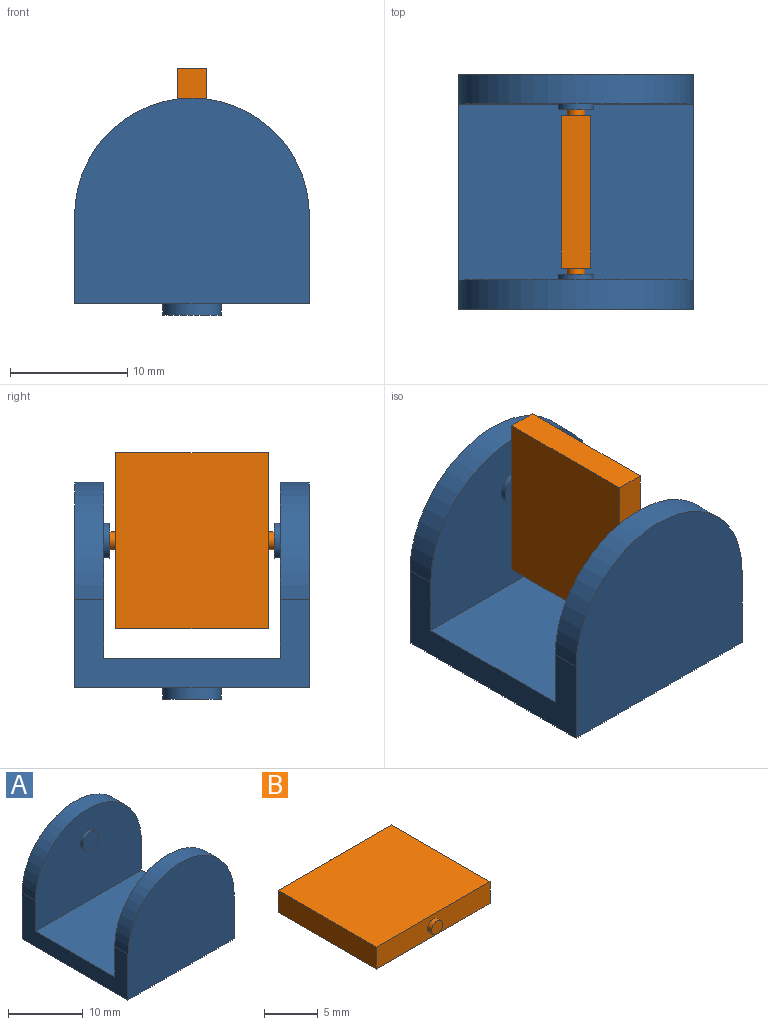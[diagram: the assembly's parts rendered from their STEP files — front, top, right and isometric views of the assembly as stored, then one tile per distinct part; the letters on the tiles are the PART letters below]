
ASSEMBLY  parts=2 mates=2
PART A: 16 faces, bbox 20x20x18.5 mm
  f0: plane 20x15mm, normal (0,0,1), area 300mm2, adj f1,f3,f6,f7
  f1: plane 20x7.5mm, normal (1,0,0), area 75mm2, adj f0,f2,f4,f5,f6,f7,f10,f11
  f2: plane 20x17.5mm, normal (0,1,0), area 307.1mm2, adj f1,f3,f5,f10
  f3: plane 20x7.5mm, normal (-1,0,0), area 75mm2, adj f0,f2,f4,f5,f6,f7,f10,f11
  f4: plane 20x17.5mm, normal (0,-1,0), area 307.1mm2, adj f1,f3,f5,f11
  f5: plane 20x20mm, normal (0,0,-1), area 380.4mm2, adj f1,f2,f3,f4,f8
  f6: plane 20x15mm, normal (0,-1,0), area 250mm2, adj f0,f1,f3,f10,f12
  f7: plane 20x15mm, normal (0,1,0), area 250mm2, adj f0,f1,f3,f11,f14
  f8: cylinder r=2.5mm len=5mm, axis (0,0,1), area 15.7mm2, adj f5,f9
  f9: plane 5x5mm, normal (0,0,-1), area 19.6mm2, adj f8
  f10: cylinder r=10mm len=20mm, axis (0,1,0), area 78.5mm2, adj f1,f2,f3,f6
  f11: cylinder r=10mm len=20mm, axis (0,1,0), area 78.5mm2, adj f1,f3,f4,f7
  f12: cylinder r=1.5mm len=3mm, axis (0,1,0), area 4.7mm2, adj f6,f13
  f13: plane 3x3mm, normal (0,-1,0), area 7.1mm2, adj f12
  f14: cylinder r=1.5mm len=3mm, axis (0,-1,0), area 4.7mm2, adj f7,f15
  f15: plane 3x3mm, normal (0,1,0), area 7.1mm2, adj f14
PART B: 10 faces, bbox 15x14x2.5 mm
  f0: plane 13x2.5mm, normal (1,0,0), area 32.5mm2, adj f1,f3,f4,f5
  f1: plane 15x2.5mm, normal (0,1,0), area 35.7mm2, adj f0,f2,f4,f5,f8
  f2: plane 13x2.5mm, normal (-1,0,0), area 32.5mm2, adj f1,f3,f4,f5
  f3: plane 15x2.5mm, normal (0,-1,0), area 35.7mm2, adj f0,f2,f4,f5,f6
  f4: plane 15x13mm, normal (0,0,1), area 195mm2, adj f0,f1,f2,f3
  f5: plane 15x13mm, normal (0,0,-1), area 195mm2, adj f0,f1,f2,f3
  f6: cylinder r=0.75mm len=1.5mm, axis (0,1,0), area 2.4mm2, adj f3,f7
  f7: plane 1.5x1.5mm, normal (0,-1,0), area 1.8mm2, adj f6
  f8: cylinder r=0.75mm len=1.5mm, axis (0,-1,0), area 2.4mm2, adj f1,f9
  f9: plane 1.5x1.5mm, normal (0,1,0), area 1.8mm2, adj f8
PLACE A at identity fixed
PLACE B rot(axis=(0,1,0),90deg) t=(-1.25,0,10)mm
MATE revolute A.f14 <-> B.f6  axis (0,1,0) through (0,-7,10)mm
MATE revolute A.f12 <-> B.f6  axis (0,-1,0) through (0,7,10)mm
